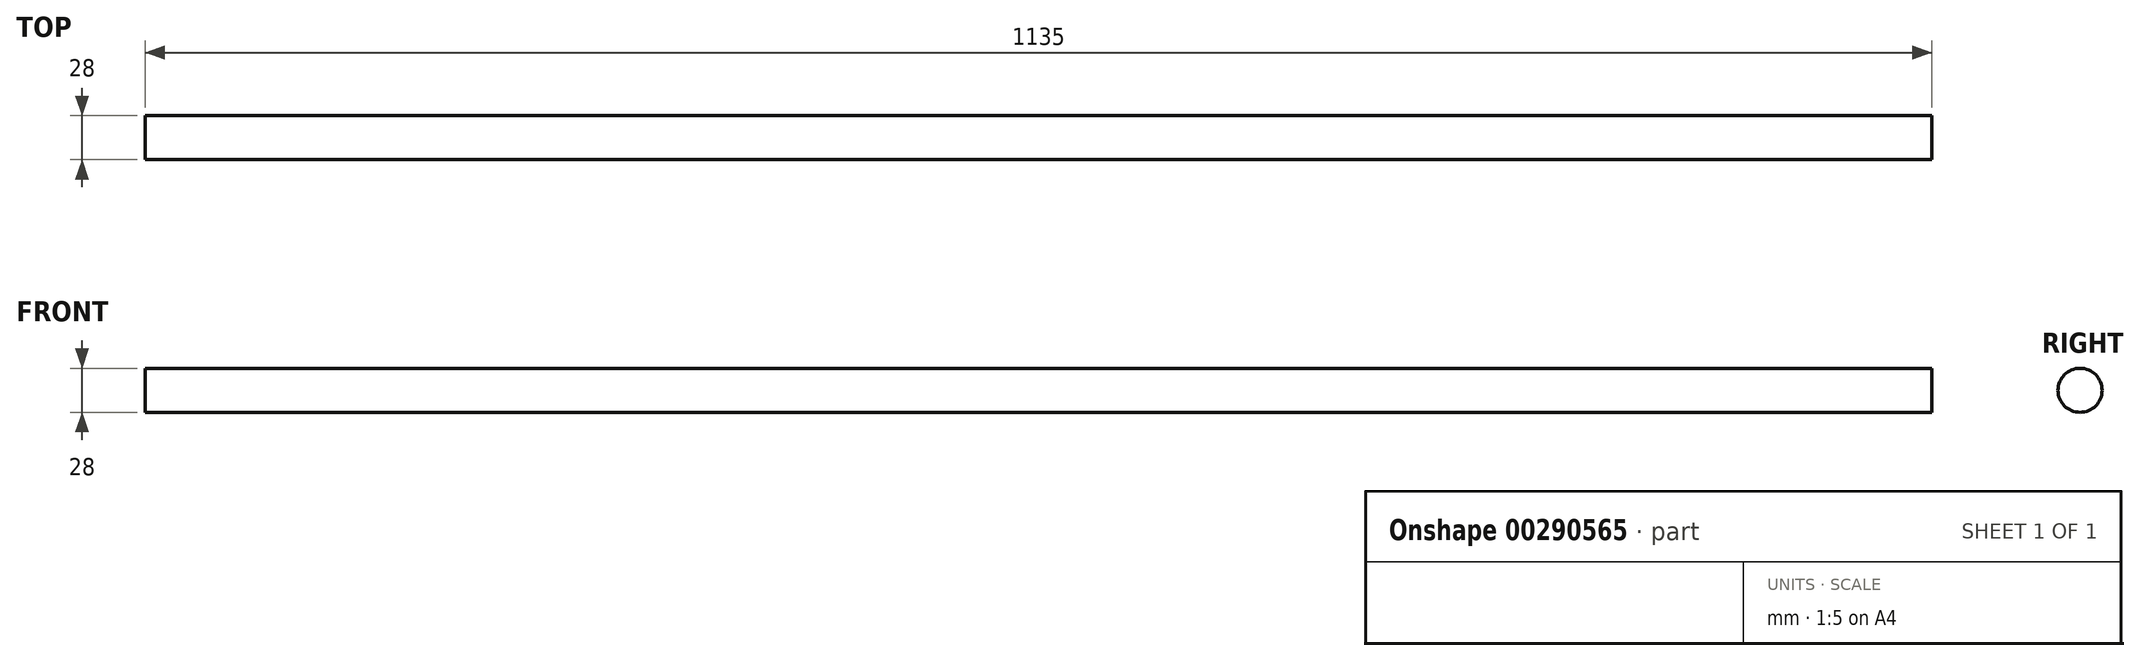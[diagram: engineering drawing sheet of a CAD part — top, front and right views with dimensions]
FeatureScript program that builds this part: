
annotation { "Feature Type Name" : "Feature", "Feature Type Description" : "" }
export const myFeature = defineFeature(function(context is Context, id is Id, definition is map)
    precondition{}
    {
        {
            var Q0;
            Q0=qCreatedBy(makeId("Right.planeOp"),FACE);
            var sketch = newSketch(context, id + "F0", { "sketchPlane" : qUnion([Q0])});
            skCircle(sketch, "E0", {"center": v(0, 0) * mm, "radius": 14 * mm});
            skSolve(sketch);
        }
        {
            var Q0;
            Q0=makeQuery(id+"F0.imprint","IMPRINT",FACE,{"disambiguationData":[TD([[makeQuery(id+"F0.imprint","IMPRINT",EDGE,{"derivedFrom":sQuery(id+"F0.wireOp",EDGE,"E0")}),1.0]])]});
            extrude(context, id + "F1", {"entities" : qUnion([Q0]), "depth" : 1135 * mm});
        }
    });
